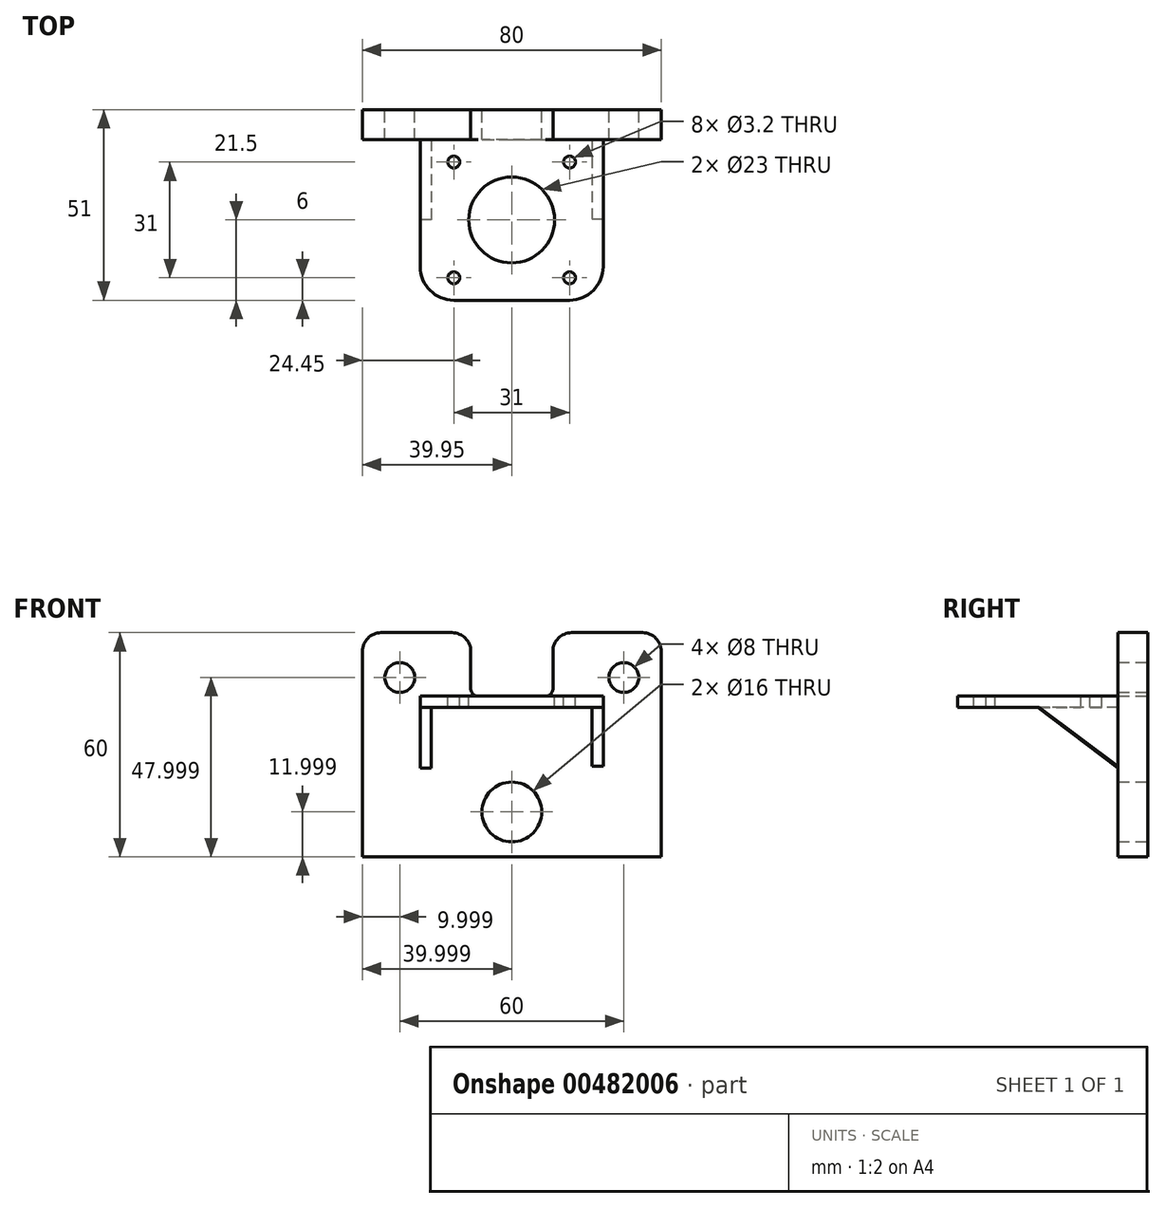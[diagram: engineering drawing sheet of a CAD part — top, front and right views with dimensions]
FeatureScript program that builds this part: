
annotation { "Feature Type Name" : "Feature", "Feature Type Description" : "" }
export const myFeature = defineFeature(function(context is Context, id is Id, definition is map)
    precondition{}
    {
        {
            var Q0;
            Q0=qCreatedBy(makeId("Front.planeOp"),FACE);
            var sketch = newSketch(context, id + "F0", { "sketchPlane" : qUnion([Q0])});
            skLineSegment(sketch, "E0", {"start": v(0.05, 175.86) * mm, "end": v(0.05, -106.38) * mm, "construction": true});
            skLineSegment(sketch, "E1.bottom", {"start": v(-34.95, 58.36) * mm, "end": v(-15.95, 58.36) * mm});
            skLineSegment(sketch, "E1.top", {"start": v(-39.95, -1.64) * mm, "end": v(-18.24, -1.64) * mm});
            skLineSegment(sketch, "E1.left", {"start": v(-39.95, 53.36) * mm, "end": v(-39.95, -1.64) * mm});
            skLineSegment(sketch, "E1.right", {"start": v(40.05, 53.36) * mm, "end": v(40.05, -1.64) * mm});
            skPoint(sketch, "E1.middle", {"position": v(0.05, 28.36) * mm});
            skCircle(sketch, "E2", {"center": v(-29.95, 46.36) * mm, "radius": 4 * mm});
            skCircle(sketch, "E3", {"center": v(30.05, 46.36) * mm, "radius": 4 * mm});
            skCircle(sketch, "E4", {"center": v(-29.95, 10.36) * mm, "radius": 5 * mm});
            skCircle(sketch, "E5", {"center": v(30.05, 10.36) * mm, "radius": 5 * mm});
            skPoint(sketch, "E6.visualSharp", {"position": v(-39.95, 58.36) * mm});
            skArc(sketch, "E6.filletArc", {"start": v(-34.95, 58.36) * mm, "mid": v(-38.49, 56.9) * mm, "end": v(-39.95, 53.36) * mm});
            skPoint(sketch, "E7.visualSharp", {"position": v(40.05, 58.36) * mm});
            skArc(sketch, "E7.filletArc", {"start": v(40.05, 53.36) * mm, "mid": v(38.58, 56.9) * mm, "end": v(35.05, 58.36) * mm});
            skLineSegment(sketch, "E8.top", {"start": v(-8.95, 41.36) * mm, "end": v(9.05, 41.36) * mm});
            skLineSegment(sketch, "E8.left", {"start": v(-10.95, 53.36) * mm, "end": v(-10.95, 43.36) * mm});
            skLineSegment(sketch, "E8.right", {"start": v(11.05, 53.36) * mm, "end": v(11.05, 43.36) * mm});
            skPoint(sketch, "E8.middle", {"position": v(0.05, 49.86) * mm});
            skPoint(sketch, "E9.visualSharp", {"position": v(11.05, 41.36) * mm});
            skArc(sketch, "E9.filletArc", {"start": v(9.05, 41.36) * mm, "mid": v(10.46, 41.94) * mm, "end": v(11.05, 43.36) * mm});
            skPoint(sketch, "E10.visualSharp", {"position": v(-10.95, 41.36) * mm});
            skArc(sketch, "E10.filletArc", {"start": v(-10.95, 43.36) * mm, "mid": v(-10.37, 41.94) * mm, "end": v(-8.95, 41.36) * mm});
            skLineSegment(sketch, "E11.trimOffspring", {"start": v(16.05, 58.36) * mm, "end": v(35.05, 58.36) * mm});
            skPoint(sketch, "E12.visualSharp", {"position": v(-10.95, 58.36) * mm});
            skArc(sketch, "E12.filletArc", {"start": v(-10.95, 53.36) * mm, "mid": v(-12.42, 56.9) * mm, "end": v(-15.95, 58.36) * mm});
            skPoint(sketch, "E13.visualSharp", {"position": v(11.05, 58.36) * mm});
            skArc(sketch, "E13.filletArc", {"start": v(16.05, 58.36) * mm, "mid": v(12.51, 56.9) * mm, "end": v(11.05, 53.36) * mm});
            skLineSegment(sketch, "E14.top", {"start": v(-13.24, 5.13) * mm, "end": v(13.34, 5.13) * mm});
            skLineSegment(sketch, "E14.left", {"start": v(-18.24, -1.64) * mm, "end": v(-18.24, 0.13) * mm});
            skLineSegment(sketch, "E14.right", {"start": v(18.34, -1.64) * mm, "end": v(18.34, 0.13) * mm});
            skPoint(sketch, "E14.middle", {"position": v(0.05, 1.74) * mm});
            skLineSegment(sketch, "E15.trimOffspring", {"start": v(18.34, -1.64) * mm, "end": v(40.05, -1.64) * mm});
            skPoint(sketch, "E16.visualSharp", {"position": v(-18.24, 5.13) * mm});
            skArc(sketch, "E16.filletArc", {"start": v(-13.24, 5.13) * mm, "mid": v(-16.77, 3.66) * mm, "end": v(-18.24, 0.13) * mm});
            skPoint(sketch, "E17.visualSharp", {"position": v(18.34, 5.13) * mm});
            skArc(sketch, "E17.filletArc", {"start": v(18.34, 0.13) * mm, "mid": v(16.87, 3.66) * mm, "end": v(13.34, 5.13) * mm});
            skLineSegment(sketch, "E18", {"start": v(18.34, -1.64) * mm, "end": v(-18.24, -1.64) * mm});
            skCircle(sketch, "E19", {"center": v(0.05, 10.36) * mm, "radius": 8 * mm});
            skSolve(sketch);
        }
        {
            var Q0;
            Q0=makeQuery(id+"F0.imprint","IMPRINT",FACE,{"disambiguationData":[TD([[makeQuery(id+"F0.imprint","IMPRINT",EDGE,{"derivedFrom":sQuery(id+"F0.wireOp",EDGE,"E1.top")}),1.0]])]});
            extrude(context, id + "F1", {"entities" : qUnion([Q0]), "depth" : 8 * mm});
        }
        {
            var Q0;
            Q0=makeQuery(id+"F1.opExtrude","SWEPT_FACE",FACE,{"disambiguationData":[OSD([sQuery(id+"F0.wireOp",EDGE,"E8.top")])]});
            var sketch = newSketch(context, id + "F2", { "sketchPlane" : qUnion([Q0])});
            skLineSegment(sketch, "E20.bottom", {"start": v(-24.49, -8) * mm, "end": v(24.51, -8) * mm});
            skLineSegment(sketch, "E20.top", {"start": v(-24.49, -51) * mm, "end": v(24.51, -51) * mm});
            skLineSegment(sketch, "E20.left", {"start": v(-24.49, -8) * mm, "end": v(-24.49, -51) * mm});
            skLineSegment(sketch, "E20.right", {"start": v(24.51, -8) * mm, "end": v(24.51, -51) * mm});
            skCircle(sketch, "E21", {"center": v(0, -29.5) * mm, "radius": 11.5 * mm});
            skPoint(sketch, "E21.centerSnap0", {"position": v(-24.49, -29.5) * mm});
            skCircle(sketch, "E22", {"center": v(-15.5, -45) * mm, "radius": 1.6 * mm});
            skCircle(sketch, "E23", {"center": v(15.5, -45) * mm, "radius": 1.6 * mm});
            skCircle(sketch, "E24", {"center": v(15.5, -14) * mm, "radius": 1.6 * mm});
            skCircle(sketch, "E25", {"center": v(-15.5, -14) * mm, "radius": 1.6 * mm});
            skLineSegment(sketch, "E26", {"start": v(-37.4, -29.5) * mm, "end": v(46.63, -29.5) * mm, "construction": true});
            skPoint(sketch, "E26.endSnap0", {"position": v(24.51, -29.5) * mm});
            skLineSegment(sketch, "E27", {"start": v(0, -70.53) * mm, "end": v(0, 44.03) * mm, "construction": true});
            skSolve(sketch);
        }
        {
            var Q0;
            Q0=qSketchRegion(id+"F2",true);
            extrude(context, id + "F3", {"entities" : qUnion([Q0]), "operationType" : NewBodyOperationType.ADD, "oppositeDirection" : true, "depth" : 3 * mm});
        }
        {
            var Q0;
            Q0=makeQuery(id+"F3.opExtrude","SWEPT_FACE",FACE,{"disambiguationData":[OSD([sQuery(id+"F2.wireOp",EDGE,"E20.left")])]});
            var sketch = newSketch(context, id + "F4", { "sketchPlane" : qUnion([Q0])});
            skLineSegment(sketch, "E28", {"start": v(8, 38.36) * mm, "end": v(29.5, 38.36) * mm});
            skLineSegment(sketch, "E29", {"start": v(29.5, 38.36) * mm, "end": v(7.88, 22.06) * mm});
            skLineSegment(sketch, "E30", {"start": v(7.88, 22.06) * mm, "end": v(8, 38.36) * mm});
            skSolve(sketch);
        }
        {
            var Q0;
            Q0=qSketchRegion(id+"F4",true);
            extrude(context, id + "F5", {"entities" : qUnion([Q0]), "operationType" : NewBodyOperationType.ADD, "oppositeDirection" : true, "depth" : 3 * mm});
        }
        {
            var Q0;
            Q0=makeQuery(id+"F3.opExtrude","SWEPT_EDGE",EDGE,{"disambiguationData":[OSD([sQuery(id+"F2.wireOp",EDGE,"E20.top"),sQuery(id+"F2.wireOp",EDGE,"E20.left")])]});
            var Q1;
            Q1=makeQuery(id+"F3.opExtrude","SWEPT_EDGE",EDGE,{"disambiguationData":[OSD([sQuery(id+"F2.wireOp",EDGE,"E20.top"),sQuery(id+"F2.wireOp",EDGE,"E20.right")])]});
            fillet(context, id + "F6", {"entities" : qUnion([Q0, Q1]), "radius" : 9 * mm, "tangentPropagation" : true, "allowEdgeOverflow" : false});
        }
        {
            var Q0;
            Q0=makeQuery(id+"F3.opExtrude","SWEPT_FACE",FACE,{"disambiguationData":[OSD([sQuery(id+"F2.wireOp",EDGE,"E20.right")])]});
            var sketch = newSketch(context, id + "F7", { "sketchPlane" : qUnion([Q0])});
            skLineSegment(sketch, "E31", {"start": v(-29.19, 38.36) * mm, "end": v(-8, 38.36) * mm});
            skLineSegment(sketch, "E32", {"start": v(-8, 38.36) * mm, "end": v(-8, 22.56) * mm});
            skLineSegment(sketch, "E33", {"start": v(-8, 22.56) * mm, "end": v(-29.19, 38.36) * mm});
            skSolve(sketch);
        }
        {
            var Q0;
            Q0=qSketchRegion(id+"F7",true);
            extrude(context, id + "F8", {"entities" : qUnion([Q0]), "operationType" : NewBodyOperationType.ADD, "oppositeDirection" : true, "depth" : 3 * mm});
        }
        {
            var Q0;
            Q0=makeQuery(id+"F0.imprint","IMPRINT",FACE,{"disambiguationData":[TD([[makeQuery(id+"F0.imprint","IMPRINT",EDGE,{"derivedFrom":sQuery(id+"F0.wireOp",EDGE,"E14.top")}),-1.0]])]});
            extrude(context, id + "F9", {"entities" : qUnion([Q0]), "operationType" : NewBodyOperationType.ADD, "depth" : 8 * mm});
        }
        {
            var Q0;
            Q0=makeQuery(id+"F0.imprint","IMPRINT",FACE,{"disambiguationData":[TD([[makeQuery(id+"F0.imprint","IMPRINT",EDGE,{"derivedFrom":sQuery(id+"F0.wireOp",EDGE,"E5")}),1.0]])]});
            var Q1;
            Q1=makeQuery(id+"F0.imprint","IMPRINT",FACE,{"disambiguationData":[TD([[makeQuery(id+"F0.imprint","IMPRINT",EDGE,{"derivedFrom":sQuery(id+"F0.wireOp",EDGE,"E4")}),1.0]])]});
            extrude(context, id + "F10", {"entities" : qUnion([Q0, Q1]), "operationType" : NewBodyOperationType.ADD, "depth" : 8 * mm});
        }
        {
            var Q0;
            Q0=makeQuery(id+"F1.opExtrude","SWEPT_BODY",BODY,{"disambiguationData":[OSD([sQuery(id+"F0.wireOp",EDGE,"E1.bottom"),sQuery(id+"F0.wireOp",EDGE,"E1.top"),sQuery(id+"F0.wireOp",EDGE,"E1.left"),sQuery(id+"F0.wireOp",EDGE,"E1.right"),sQuery(id+"F0.wireOp",EDGE,"E2"),sQuery(id+"F0.wireOp",EDGE,"E3"),sQuery(id+"F0.wireOp",EDGE,"E4"),sQuery(id+"F0.wireOp",EDGE,"E5"),sQuery(id+"F0.wireOp",EDGE,"E6.filletArc"),sQuery(id+"F0.wireOp",EDGE,"E7.filletArc"),sQuery(id+"F0.wireOp",EDGE,"E8.top"),sQuery(id+"F0.wireOp",EDGE,"E8.left"),sQuery(id+"F0.wireOp",EDGE,"E8.right"),sQuery(id+"F0.wireOp",EDGE,"E9.filletArc"),sQuery(id+"F0.wireOp",EDGE,"E10.filletArc"),sQuery(id+"F0.wireOp",EDGE,"E11.trimOffspring"),sQuery(id+"F0.wireOp",EDGE,"E12.filletArc"),sQuery(id+"F0.wireOp",EDGE,"E13.filletArc"),sQuery(id+"F0.wireOp",EDGE,"E14.top"),sQuery(id+"F0.wireOp",EDGE,"E14.left"),sQuery(id+"F0.wireOp",EDGE,"E14.right"),sQuery(id+"F0.wireOp",EDGE,"E15.trimOffspring"),sQuery(id+"F0.wireOp",EDGE,"E16.filletArc"),sQuery(id+"F0.wireOp",EDGE,"E17.filletArc"),sQuery(id+"F0.wireOp",EDGE,"E19")])]});
            transform(context, id + "F11", {"entities" : qUnion([Q0]), "transformType" : TransformType.TRANSLATION_3D, "dx" : 0 * mm, "dy" : 0 * mm, "dz" : 0 * mm, "makeCopy" : true});
        }
    });
